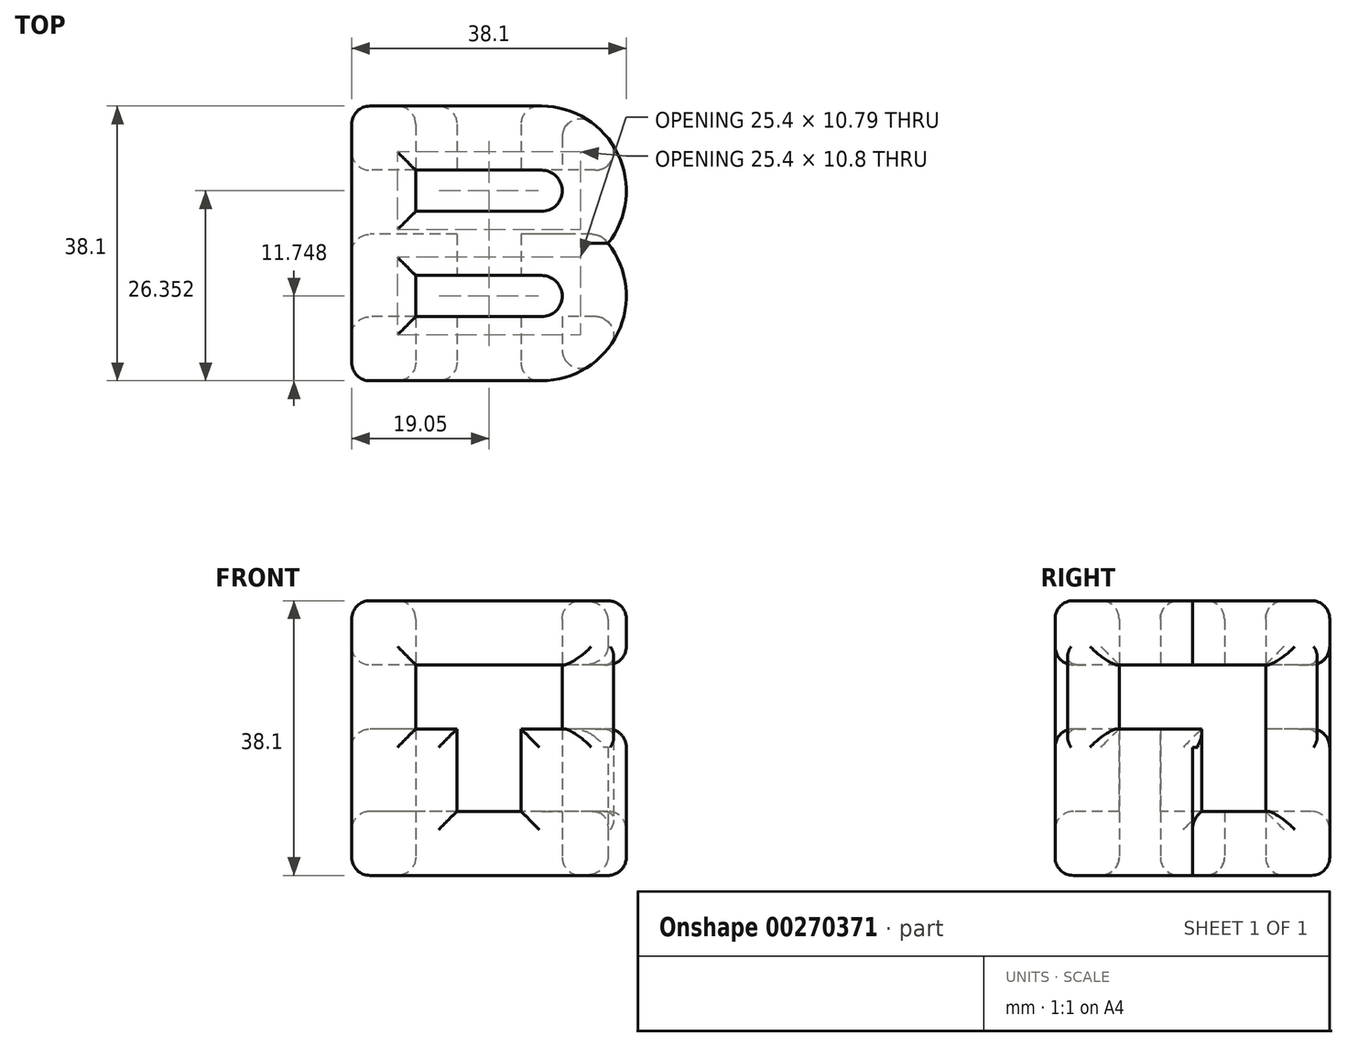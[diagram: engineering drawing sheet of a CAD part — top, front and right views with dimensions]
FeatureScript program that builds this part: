
annotation { "Feature Type Name" : "Feature", "Feature Type Description" : "" }
export const myFeature = defineFeature(function(context is Context, id is Id, definition is map)
    precondition{}
    {
        {
            var Q0;
            Q0=qCreatedBy(makeId("Top.planeOp"),FACE);
            var sketch = newSketch(context, id + "F0", { "sketchPlane" : qUnion([Q0])});
            skLineSegment(sketch, "E0", {"start": v(0, 0) * mm, "end": v(0, 38.1) * mm});
            skLineSegment(sketch, "E1", {"start": v(0, 38.1) * mm, "end": v(26.35, 38.1) * mm});
            skArc(sketch, "E2", {"start": v(26.35, 38.1) * mm, "mid": v(36.93, 31.46) * mm, "end": v(35.55, 19.05) * mm});
            skLineSegment(sketch, "E3", {"start": v(0, 0) * mm, "end": v(26.35, 0) * mm});
            skArc(sketch, "E4", {"start": v(26.35, 0) * mm, "mid": v(36.93, 6.64) * mm, "end": v(35.55, 19.05) * mm});
            skLineSegment(sketch, "E5.bottom", {"start": v(8.9, 29.21) * mm, "end": v(26.35, 29.21) * mm});
            skLineSegment(sketch, "E5.top", {"start": v(8.9, 23.5) * mm, "end": v(26.35, 23.5) * mm});
            skLineSegment(sketch, "E5.left", {"start": v(8.9, 29.21) * mm, "end": v(8.9, 23.5) * mm});
            skLineSegment(sketch, "E5.right", {"start": v(26.35, 29.21) * mm, "end": v(26.35, 23.5) * mm, "construction": true});
            skLineSegment(sketch, "E6.bottom", {"start": v(8.9, 14.6) * mm, "end": v(26.35, 14.6) * mm});
            skLineSegment(sketch, "E6.top", {"start": v(8.89, 8.9) * mm, "end": v(26.35, 8.9) * mm});
            skLineSegment(sketch, "E6.left", {"start": v(8.89, 14.6) * mm, "end": v(8.89, 8.9) * mm});
            skLineSegment(sketch, "E6.right", {"start": v(26.35, 14.6) * mm, "end": v(26.35, 8.9) * mm, "construction": true});
            skLineSegment(sketch, "E7", {"start": v(8.9, 29.21) * mm, "end": v(8.9, 38.1) * mm, "construction": true});
            skLineSegment(sketch, "E8", {"start": v(8.9, 29.21) * mm, "end": v(0, 29.21) * mm, "construction": true});
            skLineSegment(sketch, "E9", {"start": v(26.35, 38.1) * mm, "end": v(38.1, 38.1) * mm, "construction": true});
            skLineSegment(sketch, "E10", {"start": v(38.1, 38.1) * mm, "end": v(38.1, 0) * mm, "construction": true});
            skLineSegment(sketch, "E11", {"start": v(38.1, 0) * mm, "end": v(0, 0) * mm, "construction": true});
            skArc(sketch, "E12", {"start": v(26.35, 23.5) * mm, "mid": v(29.21, 26.35) * mm, "end": v(26.35, 29.21) * mm});
            skArc(sketch, "E13", {"start": v(26.35, 14.6) * mm, "mid": v(29.21, 11.75) * mm, "end": v(26.35, 8.9) * mm});
            skLineSegment(sketch, "E14", {"start": v(8.9, 23.5) * mm, "end": v(8.9, 14.6) * mm, "construction": true});
            skSolve(sketch);
        }
        {
            var Q0;
            Q0=makeQuery(id+"F0.imprint","IMPRINT",FACE,{"disambiguationData":[TD([[makeQuery(id+"F0.imprint","IMPRINT",EDGE,{"derivedFrom":sQuery(id+"F0.wireOp",EDGE,"E0")}),-1.0]])]});
            extrude(context, id + "F1", {"entities" : qUnion([Q0]), "depth" : 38.1 * mm});
        }
        {
            var Q0;
            Q0=qCreatedBy(makeId("Front.planeOp"),FACE);
            var sketch = newSketch(context, id + "F2", { "sketchPlane" : qUnion([Q0])});
            skLineSegment(sketch, "E15.bottom", {"start": v(8.89, 29.21) * mm, "end": v(29.2, 29.21) * mm});
            skLineSegment(sketch, "E15.top", {"start": v(8.89, 20.32) * mm, "end": v(14.6, 20.32) * mm});
            skLineSegment(sketch, "E15.left", {"start": v(8.9, 29.21) * mm, "end": v(8.9, 20.32) * mm});
            skLineSegment(sketch, "E15.right", {"start": v(29.2, 29.21) * mm, "end": v(29.2, 20.32) * mm});
            skLineSegment(sketch, "E16.top", {"start": v(14.6, 8.9) * mm, "end": v(23.5, 8.9) * mm});
            skLineSegment(sketch, "E16.left", {"start": v(14.6, 20.32) * mm, "end": v(14.6, 8.9) * mm});
            skLineSegment(sketch, "E16.right", {"start": v(23.5, 20.32) * mm, "end": v(23.5, 8.9) * mm});
            skLineSegment(sketch, "E17", {"start": v(19.05, 8.9) * mm, "end": v(19.05, 0) * mm, "construction": true});
            skLineSegment(sketch, "E18", {"start": v(19.05, 20.32) * mm, "end": v(19.05, 29.21) * mm, "construction": true});
            skLineSegment(sketch, "E19.trimOffspring", {"start": v(23.5, 20.32) * mm, "end": v(29.2, 20.32) * mm});
            skLineSegment(sketch, "E20", {"start": v(14.6, 20.32) * mm, "end": v(23.5, 20.32) * mm, "construction": true});
            skLineSegment(sketch, "E21", {"start": v(8.89, 29.21) * mm, "end": v(0, 29.21) * mm, "construction": true});
            skLineSegment(sketch, "E22", {"start": v(8.9, 29.21) * mm, "end": v(8.9, 38.1) * mm, "construction": true});
            skSolve(sketch);
        }
        {
            var Q0;
            Q0 = qSketchRegion(id + "F2", true);
            extrude(context, id + "F3", {"entities" : qUnion([Q0]), "operationType" : NewBodyOperationType.REMOVE, "endBound" : BoundingType.THROUGH_ALL, "oppositeDirection" : true, "depth" : 25.4 * mm});
        }
        {
            var Q0;
            Q0=makeQuery(id+"F1.opExtrude","SWEPT_FACE",FACE,{"disambiguationData":[OSD([sQuery(id+"F0.wireOp",EDGE,"E0")])]});
            var sketch = newSketch(context, id + "F4", { "sketchPlane" : qUnion([Q0])});
            skLineSegment(sketch, "E23", {"start": v(-29.21, 29.21) * mm, "end": v(-29.21, 8.9) * mm});
            skLineSegment(sketch, "E24", {"start": v(-29.2, 29.21) * mm, "end": v(-8.9, 29.21) * mm});
            skLineSegment(sketch, "E25", {"start": v(-8.9, 20.32) * mm, "end": v(-8.9, 29.21) * mm});
            skLineSegment(sketch, "E26", {"start": v(-8.9, 20.32) * mm, "end": v(-20.32, 20.32) * mm});
            skLineSegment(sketch, "E27", {"start": v(-20.32, 8.9) * mm, "end": v(-20.32, 20.32) * mm});
            skLineSegment(sketch, "E28", {"start": v(-20.32, 8.9) * mm, "end": v(-29.2, 8.9) * mm});
            skLineSegment(sketch, "E29", {"start": v(-29.21, 19.05) * mm, "end": v(-38.1, 19.05) * mm, "construction": true});
            skLineSegment(sketch, "E30", {"start": v(-19.05, 29.21) * mm, "end": v(-19.05, 38.1) * mm, "construction": true});
            skPoint(sketch, "E30.startSnap0", {"position": v(-19.05, 38.1) * mm});
            skSolve(sketch);
        }
        {
            var Q0;
            Q0 = qSketchRegion(id + "F4", true);
            extrude(context, id + "F5", {"entities" : qUnion([Q0]), "operationType" : NewBodyOperationType.REMOVE, "endBound" : BoundingType.THROUGH_ALL, "oppositeDirection" : true, "depth" : 25.4 * mm});
        }
        {
            var Q0;
            Q0=makeQuery(id+"F1.opExtrude","CAP_FACE",FACE,{"disambiguationData":[OSD([sQuery(id+"F0.wireOp",EDGE,"E0"),sQuery(id+"F0.wireOp",EDGE,"E1"),sQuery(id+"F0.wireOp",EDGE,"E2"),sQuery(id+"F0.wireOp",EDGE,"E3"),sQuery(id+"F0.wireOp",EDGE,"E4"),sQuery(id+"F0.wireOp",EDGE,"E5.bottom"),sQuery(id+"F0.wireOp",EDGE,"E5.top"),sQuery(id+"F0.wireOp",EDGE,"E5.left"),sQuery(id+"F0.wireOp",EDGE,"E6.bottom"),sQuery(id+"F0.wireOp",EDGE,"E6.top"),sQuery(id+"F0.wireOp",EDGE,"E6.left"),sQuery(id+"F0.wireOp",EDGE,"E12"),sQuery(id+"F0.wireOp",EDGE,"E13")])],"isStart":true});
            var Q1;
            Q1=makeQuery(id+"F1.opExtrude","SWEPT_FACE",FACE,{"disambiguationData":[OSD([sQuery(id+"F0.wireOp",EDGE,"E0")])]});
            var Q2;
            Q2=makeQuery(id+"F1.opExtrude","CAP_FACE",FACE,{"disambiguationData":[OSD([sQuery(id+"F0.wireOp",EDGE,"E0"),sQuery(id+"F0.wireOp",EDGE,"E1"),sQuery(id+"F0.wireOp",EDGE,"E2"),sQuery(id+"F0.wireOp",EDGE,"E3"),sQuery(id+"F0.wireOp",EDGE,"E4"),sQuery(id+"F0.wireOp",EDGE,"E5.bottom"),sQuery(id+"F0.wireOp",EDGE,"E5.top"),sQuery(id+"F0.wireOp",EDGE,"E5.left"),sQuery(id+"F0.wireOp",EDGE,"E6.bottom"),sQuery(id+"F0.wireOp",EDGE,"E6.top"),sQuery(id+"F0.wireOp",EDGE,"E6.left"),sQuery(id+"F0.wireOp",EDGE,"E12"),sQuery(id+"F0.wireOp",EDGE,"E13")])],"isStart":false});
            var Q3;
            Q3=makeQuery(id+"F1.opExtrude","SWEPT_FACE",FACE,{"disambiguationData":[OSD([sQuery(id+"F0.wireOp",EDGE,"E3")])]});
            var Q4;
            Q4=makeQuery(id+"F3.boolean.opBoolean","INTERSECT",EDGE,{"derivedFrom":[makeQuery(id+"F1.opExtrude","SWEPT_FACE",FACE,{"disambiguationData":[OSD([sQuery(id+"F0.wireOp",EDGE,"E4")])]}),makeQuery(id+"F3.opExtrude","SWEPT_FACE",FACE,{"disambiguationData":[OSD([sQuery(id+"F2.wireOp",EDGE,"E15.right")])]})]});
            var Q5;
            Q5=makeQuery(id+"F1.opExtrude","SWEPT_FACE",FACE,{"disambiguationData":[OSD([sQuery(id+"F0.wireOp",EDGE,"E1")])]});
            var Q6;
            Q6=makeQuery(id+"F3.boolean.opBoolean","INTERSECT",EDGE,{"derivedFrom":[makeQuery(id+"F1.opExtrude","SWEPT_FACE",FACE,{"disambiguationData":[OSD([sQuery(id+"F0.wireOp",EDGE,"E2")])]}),makeQuery(id+"F3.opExtrude","SWEPT_FACE",FACE,{"disambiguationData":[OSD([sQuery(id+"F2.wireOp",EDGE,"E15.right")])]})]});
            var Q7;
            Q7=makeQuery(id+"F5.boolean.opBoolean","INTERSECT",EDGE,{"derivedFrom":[makeQuery(id+"F1.opExtrude","SWEPT_FACE",FACE,{"disambiguationData":[OSD([sQuery(id+"F0.wireOp",EDGE,"E2")])]}),makeQuery(id+"F5.opExtrude","SWEPT_FACE",FACE,{"disambiguationData":[OSD([sQuery(id+"F4.wireOp",EDGE,"E23")])]})]});
            var Q8;
            Q8=makeQuery(id+"F5.boolean.opBoolean","INTERSECT",EDGE,{"derivedFrom":[makeQuery(id+"F1.opExtrude","SWEPT_FACE",FACE,{"disambiguationData":[OSD([sQuery(id+"F0.wireOp",EDGE,"E2")])]}),makeQuery(id+"F5.opExtrude","SWEPT_FACE",FACE,{"disambiguationData":[OSD([sQuery(id+"F4.wireOp",EDGE,"E24")])]})]});
            var Q9;
            Q9=makeQuery(id+"F5.boolean.opBoolean","INTERSECT",EDGE,{"derivedFrom":[makeQuery(id+"F1.opExtrude","SWEPT_FACE",FACE,{"disambiguationData":[OSD([sQuery(id+"F0.wireOp",EDGE,"E2")])]}),makeQuery(id+"F5.opExtrude","SWEPT_FACE",FACE,{"disambiguationData":[OSD([sQuery(id+"F4.wireOp",EDGE,"E28")])]})]});
            var Q10;
            Q10=makeQuery(id+"F5.boolean.opBoolean","INTERSECT",EDGE,{"derivedFrom":[makeQuery(id+"F1.opExtrude","SWEPT_FACE",FACE,{"disambiguationData":[OSD([sQuery(id+"F0.wireOp",EDGE,"E2")])]}),makeQuery(id+"F5.opExtrude","SWEPT_FACE",FACE,{"disambiguationData":[OSD([sQuery(id+"F4.wireOp",EDGE,"E27")])]})]});
            var Q11;
            Q11=makeQuery(id+"F5.boolean.opBoolean","INTERSECT",EDGE,{"derivedFrom":[makeQuery(id+"F1.opExtrude","SWEPT_FACE",FACE,{"disambiguationData":[OSD([sQuery(id+"F0.wireOp",EDGE,"E4")])]}),makeQuery(id+"F5.opExtrude","SWEPT_FACE",FACE,{"disambiguationData":[OSD([sQuery(id+"F4.wireOp",EDGE,"E25")])]})]});
            var Q12;
            Q12=makeQuery(id+"F5.boolean.opBoolean","INTERSECT",EDGE,{"derivedFrom":[makeQuery(id+"F1.opExtrude","SWEPT_FACE",FACE,{"disambiguationData":[OSD([sQuery(id+"F0.wireOp",EDGE,"E4")])]}),makeQuery(id+"F5.opExtrude","SWEPT_FACE",FACE,{"disambiguationData":[OSD([sQuery(id+"F4.wireOp",EDGE,"E24")])]})]});
            fillet(context, id + "F6", {"entities" : qUnion([Q0, Q1, Q2, Q3, Q4, Q5, Q6, Q7, Q8, Q9, Q10, Q11, Q12]), "radius" : 2.54 * mm, "tangentPropagation" : true, "allowEdgeOverflow" : false});
        }
        {
            var Q0;
            Q0=makeQuery(id+"F5.boolean.opBoolean","INTERSECT",EDGE,{"derivedFrom":[makeQuery(id+"F1.opExtrude","SWEPT_FACE",FACE,{"disambiguationData":[OSD([sQuery(id+"F0.wireOp",EDGE,"E4")])]}),makeQuery(id+"F5.opExtrude","SWEPT_FACE",FACE,{"disambiguationData":[OSD([sQuery(id+"F4.wireOp",EDGE,"E26")])]})]});
            fillet(context, id + "F7", {"entities" : qUnion([Q0]), "radius" : 2.54 * mm, "tangentPropagation" : true, "allowEdgeOverflow" : false});
        }
        {
            var Q0;
            Q0=makeQuery(id+"F1.opExtrude","SWEPT_FACE",FACE,{"disambiguationData":[OSD([sQuery(id+"F0.wireOp",EDGE,"E3")])]});
            var Q1;
            Q1=sQuery(id+"F0.wireOp",VERTEX,"E4.center");
            cPlane(context, id + "F8", {"entities" : qUnion([Q0, Q1]), "cplaneType" : CPlaneType.PLANE_POINT, "offset" : 25.4 * mm, "width" : 152.4 * mm, "height" : 152.4 * mm});
        }
        {
            var Q0;
            Q0=qCreatedBy(id+"F8.planeOp",FACE);
            var sketch = newSketch(context, id + "F9", { "sketchPlane" : qUnion([Q0])});
            skArc(sketch, "E31", {"start": v(38.1, 17.78) * mm, "mid": v(37.35, 19.58) * mm, "end": v(35.56, 20.32) * mm});
            skLineSegment(sketch, "E32", {"start": v(35.56, 17.78) * mm, "end": v(38.1, 17.78) * mm, "construction": true});
            skLineSegment(sketch, "E33", {"start": v(35.56, 20.32) * mm, "end": v(35.56, 17.78) * mm, "construction": true});
            skLineSegment(sketch, "E34", {"start": v(26.35, 11.72) * mm, "end": v(26.35, 23) * mm});
            skLineSegment(sketch, "E35", {"start": v(38.1, 17.78) * mm, "end": v(39.85, 16.78) * mm});
            skLineSegment(sketch, "E36", {"start": v(39.85, 16.78) * mm, "end": v(39.85, 23.55) * mm});
            skLineSegment(sketch, "E37", {"start": v(39.85, 23.55) * mm, "end": v(35.56, 20.32) * mm});
            skSolve(sketch);
        }
        {
            var Q0;
            Q0=makeQuery(id+"F9.imprint","IMPRINT",FACE,{"disambiguationData":[TD([[makeQuery(id+"F9.imprint","IMPRINT",EDGE,{"derivedFrom":sQuery(id+"F9.wireOp",EDGE,"E31")}),-1.0]])]});
            var Q1;
            Q1=sQuery(id+"F9.wireOp",EDGE,"E34");
            revolve(context, id + "F10", {"operationType" : NewBodyOperationType.REMOVE, "entities" : qUnion([Q0]), "axis" : qUnion([Q1]), "revolveType" : RevolveType.ONE_DIRECTION, "angle" : 75 * degree});
        }
    });
